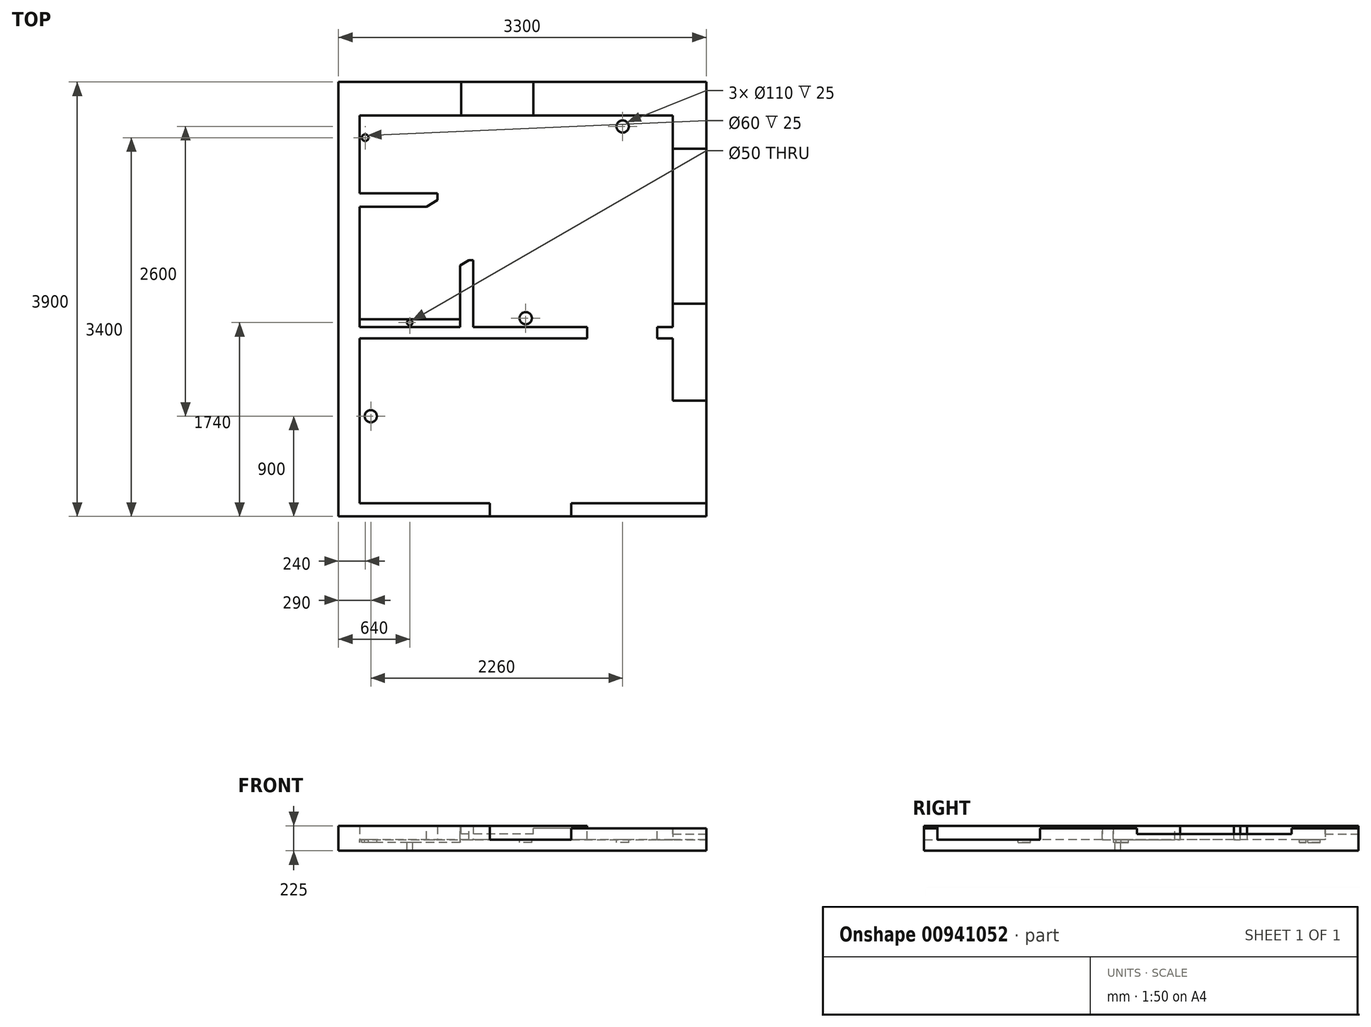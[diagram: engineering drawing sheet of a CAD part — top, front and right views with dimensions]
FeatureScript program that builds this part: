
annotation { "Feature Type Name" : "Feature", "Feature Type Description" : "" }
export const myFeature = defineFeature(function(context is Context, id is Id, definition is map)
    precondition{}
    {
        {
            var Q0;
            Q0=qCreatedBy(makeId("Top.planeOp"),FACE);
            var sketch = newSketch(context, id + "F0", { "sketchPlane" : qUnion([Q0])});
            skLineSegment(sketch, "E0.bottom", {"start": v(0, 0) * mm, "end": v(-3300, 0) * mm});
            skLineSegment(sketch, "E0.top", {"start": v(0, -3900) * mm, "end": v(-3300, -3900) * mm});
            skLineSegment(sketch, "E0.left", {"start": v(0, 0) * mm, "end": v(0, -3900) * mm});
            skLineSegment(sketch, "E0.right", {"start": v(-3300, 0) * mm, "end": v(-3300, -3900) * mm});
            skSolve(sketch);
        }
        {
            var Q0;
            Q0=qSketchRegion(id+"F0",true);
            extrude(context, id + "F1", {"entities" : qUnion([Q0]), "oppositeDirection" : true, "depth" : 100 * mm, "offsetDistance" : 25 * mm});
        }
        {
            var Q0;
            Q0=makeQuery(id+"F0.imprint","IMPRINT",FACE,{"disambiguationData":[TD([[makeQuery(id+"F0.imprint","IMPRINT",EDGE,{"derivedFrom":sQuery(id+"F0.wireOp",EDGE,"E0.bottom")}),1.0]])]});
            var sketch = newSketch(context, id + "F2", { "sketchPlane" : qUnion([Q0])});
            skLineSegment(sketch, "E1.bottom", {"start": v(-300, -300) * mm, "end": v(-1450, -300) * mm});
            skLineSegment(sketch, "E1.top", {"start": v(-300, -2200) * mm, "end": v(-1450, -2200) * mm});
            skLineSegment(sketch, "E1.left", {"start": v(-300, -300) * mm, "end": v(-300, -2200) * mm});
            skLineSegment(sketch, "E1.right", {"start": v(-1450, -300) * mm, "end": v(-1450, -2200) * mm});
            skLineSegment(sketch, "E2.bottom", {"start": v(-1550, -300) * mm, "end": v(-3110, -300) * mm});
            skLineSegment(sketch, "E2.top", {"start": v(-1550, -2200) * mm, "end": v(-3110, -2200) * mm});
            skLineSegment(sketch, "E2.left", {"start": v(-1550, -300) * mm, "end": v(-1550, -2200) * mm});
            skLineSegment(sketch, "E2.right", {"start": v(-3110, -300) * mm, "end": v(-3110, -2200) * mm});
            skLineSegment(sketch, "E3.bottom", {"start": v(-3110, -2300) * mm, "end": v(-300, -2300) * mm});
            skLineSegment(sketch, "E3.top", {"start": v(-3110, -3780) * mm, "end": v(-300, -3780) * mm});
            skLineSegment(sketch, "E3.left", {"start": v(-3110, -2300) * mm, "end": v(-3110, -3780) * mm});
            skLineSegment(sketch, "E3.right", {"start": v(-300, -2300) * mm, "end": v(-300, -3780) * mm});
            skLineSegment(sketch, "E4.bottom", {"start": v(0, 0) * mm, "end": v(-3300, 0) * mm});
            skLineSegment(sketch, "E4.top", {"start": v(0, -3900) * mm, "end": v(-3300, -3900) * mm});
            skLineSegment(sketch, "E4.left", {"start": v(0, 0) * mm, "end": v(0, -3900) * mm});
            skLineSegment(sketch, "E4.right", {"start": v(-3300, 0) * mm, "end": v(-3300, -3900) * mm});
            skSolve(sketch);
        }
        {
            var Q0;
            Q0=qSketchRegion(id+"F2",true);
            extrude(context, id + "F3", {"entities" : qUnion([Q0]), "operationType" : NewBodyOperationType.ADD, "depth" : 100 * mm, "offsetDistance" : 25 * mm});
        }
        {
            var Q0;
            Q0=makeQuery(id+"F3.opExtrude","CAP_FACE",FACE,{"disambiguationData":[OSD([sQuery(id+"F2.wireOp",EDGE,"E1.bottom"),sQuery(id+"F2.wireOp",EDGE,"E1.top"),sQuery(id+"F2.wireOp",EDGE,"E1.left"),sQuery(id+"F2.wireOp",EDGE,"E1.right"),sQuery(id+"F2.wireOp",EDGE,"E2.bottom"),sQuery(id+"F2.wireOp",EDGE,"E2.top"),sQuery(id+"F2.wireOp",EDGE,"E2.left"),sQuery(id+"F2.wireOp",EDGE,"E2.right"),sQuery(id+"F2.wireOp",EDGE,"E3.bottom"),sQuery(id+"F2.wireOp",EDGE,"E3.top"),sQuery(id+"F2.wireOp",EDGE,"E3.left"),sQuery(id+"F2.wireOp",EDGE,"E3.right"),sQuery(id+"F2.wireOp",EDGE,"E4.bottom"),sQuery(id+"F2.wireOp",EDGE,"E4.top"),sQuery(id+"F2.wireOp",EDGE,"E4.left"),sQuery(id+"F2.wireOp",EDGE,"E4.right")])],"isStart":false});
            var sketch = newSketch(context, id + "F4", { "sketchPlane" : qUnion([Q0])});
            skLineSegment(sketch, "E5.bottom", {"start": v(-1550, -300) * mm, "end": v(-2200, -300) * mm});
            skLineSegment(sketch, "E5.top", {"start": v(-1550, 0) * mm, "end": v(-2200, 0) * mm});
            skLineSegment(sketch, "E5.left", {"start": v(-1550, -300) * mm, "end": v(-1550, 0) * mm});
            skLineSegment(sketch, "E5.right", {"start": v(-2200, -300) * mm, "end": v(-2200, 0) * mm});
            skLineSegment(sketch, "E6.bottom", {"start": v(-300, -600) * mm, "end": v(0, -600) * mm});
            skLineSegment(sketch, "E6.top", {"start": v(-300, -1990) * mm, "end": v(0, -1990) * mm});
            skLineSegment(sketch, "E6.left", {"start": v(-300, -600) * mm, "end": v(-300, -1990) * mm});
            skLineSegment(sketch, "E6.right", {"start": v(0, -600) * mm, "end": v(0, -1990) * mm});
            skLineSegment(sketch, "E7.bottom", {"start": v(-440, -2200) * mm, "end": v(-1070, -2200) * mm});
            skLineSegment(sketch, "E7.top", {"start": v(-440, -2300) * mm, "end": v(-1070, -2300) * mm});
            skLineSegment(sketch, "E7.left", {"start": v(-440, -2200) * mm, "end": v(-440, -2300) * mm});
            skLineSegment(sketch, "E7.right", {"start": v(-1070, -2200) * mm, "end": v(-1070, -2300) * mm});
            skLineSegment(sketch, "E8.bottom", {"start": v(-1770, -2200) * mm, "end": v(-2400, -2200) * mm});
            skLineSegment(sketch, "E8.top", {"start": v(-1770, -2300) * mm, "end": v(-2400, -2300) * mm});
            skLineSegment(sketch, "E8.left", {"start": v(-1770, -2200) * mm, "end": v(-1770, -2300) * mm});
            skLineSegment(sketch, "E8.right", {"start": v(-2400, -2200) * mm, "end": v(-2400, -2300) * mm});
            skLineSegment(sketch, "E9.bottom", {"start": v(-1210, -3780) * mm, "end": v(-1940, -3780) * mm});
            skLineSegment(sketch, "E9.top", {"start": v(-1210, -3900) * mm, "end": v(-1940, -3900) * mm});
            skLineSegment(sketch, "E9.left", {"start": v(-1210, -3780) * mm, "end": v(-1210, -3900) * mm});
            skLineSegment(sketch, "E9.right", {"start": v(-1940, -3780) * mm, "end": v(-1940, -3900) * mm});
            skLineSegment(sketch, "E10.bottom", {"start": v(-300, -2860) * mm, "end": v(0, -2860) * mm});
            skLineSegment(sketch, "E10.top", {"start": v(-300, -3780) * mm, "end": v(0, -3780) * mm});
            skLineSegment(sketch, "E10.left", {"start": v(-300, -2860) * mm, "end": v(-300, -3780) * mm});
            skLineSegment(sketch, "E10.right", {"start": v(0, -2860) * mm, "end": v(0, -3780) * mm});
            skSolve(sketch);
        }
        {
            var Q0;
            Q0=makeQuery(id+"F4.imprint","IMPRINT",FACE,{"disambiguationData":[TD([[makeQuery(id+"F4.imprint","IMPRINT",EDGE,{"derivedFrom":sQuery(id+"F4.wireOp",EDGE,"E8.bottom")}),1.0]])]});
            var Q1;
            Q1=makeQuery(id+"F4.imprint","IMPRINT",FACE,{"disambiguationData":[TD([[makeQuery(id+"F4.imprint","IMPRINT",EDGE,{"derivedFrom":sQuery(id+"F4.wireOp",EDGE,"E7.bottom")}),1.0]])]});
            var Q2;
            Q2=makeQuery(id+"F4.imprint","IMPRINT",FACE,{"disambiguationData":[TD([[makeQuery(id+"F4.imprint","IMPRINT",EDGE,{"derivedFrom":sQuery(id+"F4.wireOp",EDGE,"E10.bottom")}),-1.0]])]});
            var Q3;
            Q3=makeQuery(id+"F4.imprint","IMPRINT",FACE,{"disambiguationData":[TD([[makeQuery(id+"F4.imprint","IMPRINT",EDGE,{"derivedFrom":sQuery(id+"F4.wireOp",EDGE,"E9.bottom")}),-1.0]])]});
            var Q4;
            Q4=makeQuery(id+"F3.boolean.opBoolean","SPLIT",FACE,{"disambiguationData":[TD([makeQuery(id+"F3.opExtrude","SWEPT_FACE",FACE,{"disambiguationData":[OSD([sQuery(id+"F2.wireOp",EDGE,"E3.bottom")])]})])],"derivedFrom":makeQuery(id+"F1.opExtrude","CAP_FACE",FACE,{"disambiguationData":[OSD([sQuery(id+"F0.wireOp",EDGE,"E0.bottom"),sQuery(id+"F0.wireOp",EDGE,"E0.top"),sQuery(id+"F0.wireOp",EDGE,"E0.left"),sQuery(id+"F0.wireOp",EDGE,"E0.right")])],"isStart":true})});
            extrude(context, id + "F5", {"entities" : qUnion([Q0, Q1, Q2, Q3]), "operationType" : NewBodyOperationType.REMOVE, "endBound" : BoundingType.UP_TO_SURFACE, "oppositeDirection" : true, "depth" : 25 * mm, "endBoundEntityFace" : qUnion([Q4]), "offsetDistance" : 25 * mm});
        }
        {
            var Q0;
            Q0=makeQuery(id+"F4.imprint","IMPRINT",FACE,{"disambiguationData":[TD([[makeQuery(id+"F4.imprint","IMPRINT",EDGE,{"derivedFrom":sQuery(id+"F4.wireOp",EDGE,"E5.bottom")}),-1.0]])]});
            var Q1;
            Q1=makeQuery(id+"F4.imprint","IMPRINT",FACE,{"disambiguationData":[TD([[makeQuery(id+"F4.imprint","IMPRINT",EDGE,{"derivedFrom":sQuery(id+"F4.wireOp",EDGE,"E6.bottom")}),-1.0]])]});
            extrude(context, id + "F6", {"entities" : qUnion([Q0, Q1]), "operationType" : NewBodyOperationType.REMOVE, "oppositeDirection" : true, "depth" : 50 * mm, "offsetDistance" : 25 * mm});
        }
        {
            var Q0;
            {var subQ0=sQuery(id+"F2.wireOp",EDGE,"E2.left");var subQ2=sQuery(id+"F2.wireOp",EDGE,"E2.top");var subQ4=sQuery(id+"F2.wireOp",EDGE,"E1.right");var subQ6=sQuery(id+"F2.wireOp",EDGE,"E1.left");var subQ9=sQuery(id+"F2.wireOp",EDGE,"E3.bottom");var subQ11=makeQuery(id+"F1.opExtrude","SWEPT_FACE",FACE,{"disambiguationData":[OSD([sQuery(id+"F0.wireOp",EDGE,"E0.bottom")])]});var subQ12=sQuery(id+"F2.wireOp",EDGE,"E1.bottom");var subQ13=makeQuery(id+"F3.opExtrude","SWEPT_FACE",FACE,{"disambiguationData":[OSD([subQ12])]});var subQ15=sQuery(id+"F2.wireOp",EDGE,"E4.bottom");var subQ17=sQuery(id+"F2.wireOp",EDGE,"E1.top");var subQ20=sQuery(id+"F2.wireOp",EDGE,"E4.left");var subQ22=sQuery(id+"F2.wireOp",EDGE,"E3.top");var subQ23=sQuery(id+"F2.wireOp",EDGE,"E4.right");var subQ24=sQuery(id+"F2.wireOp",EDGE,"E4.top");var subQ25=sQuery(id+"F2.wireOp",EDGE,"E3.right");var subQ26=sQuery(id+"F2.wireOp",EDGE,"E3.left");var subQ27=sQuery(id+"F2.wireOp",EDGE,"E2.right");var subQ28=sQuery(id+"F2.wireOp",EDGE,"E2.bottom");Q0=makeQuery(id+"F6.boolean.opBoolean","SPLIT",FACE,{"disambiguationData":[TD([subQ13])],"derivedFrom":makeQuery(id+"F5.boolean.opBoolean","SPLIT",FACE,{"disambiguationData":[TD([subQ11])],"derivedFrom":makeQuery(id+"F3.opExtrude","CAP_FACE",FACE,{"disambiguationData":[OSD([subQ12,subQ17,subQ6,subQ4,subQ28,subQ2,subQ0,subQ27,subQ9,subQ22,subQ26,subQ25,subQ15,subQ24,subQ20,subQ23])],"isStart":false})})});}
            var sketch = newSketch(context, id + "F7", { "sketchPlane" : qUnion([Q0])});
            skLineSegment(sketch, "E11.bottom", {"start": v(-1450, -300) * mm, "end": v(-1550, -300) * mm});
            skLineSegment(sketch, "E11.top", {"start": v(-1450, -2200) * mm, "end": v(-1550, -2200) * mm});
            skLineSegment(sketch, "E11.left", {"start": v(-1450, -300) * mm, "end": v(-1450, -2200) * mm});
            skLineSegment(sketch, "E11.right", {"start": v(-1550, -300) * mm, "end": v(-1550, -2200) * mm});
            skSolve(sketch);
        }
        {
            var Q0;
            Q0 = qSketchRegion(id + "F7", true);
            var Q1;
            {var subQ0=makeQuery(id+"F1.opExtrude","CAP_FACE",FACE,{"disambiguationData":[OSD([sQuery(id+"F0.wireOp",EDGE,"E0.bottom"),sQuery(id+"F0.wireOp",EDGE,"E0.top"),sQuery(id+"F0.wireOp",EDGE,"E0.left"),sQuery(id+"F0.wireOp",EDGE,"E0.right")])],"isStart":true});Q1=makeQuery(id+"F5.boolean.opBoolean","MERGE",FACE,{"derivedFrom":[makeQuery(id+"F3.boolean.opBoolean","SPLIT",FACE,{"disambiguationData":[TD([makeQuery(id+"F3.opExtrude","SWEPT_FACE",FACE,{"disambiguationData":[OSD([sQuery(id+"F2.wireOp",EDGE,"E1.bottom")])]})])],"derivedFrom":subQ0}),makeQuery(id+"F3.boolean.opBoolean","SPLIT",FACE,{"disambiguationData":[TD([makeQuery(id+"F3.opExtrude","SWEPT_FACE",FACE,{"disambiguationData":[OSD([sQuery(id+"F2.wireOp",EDGE,"E2.bottom")])]})])],"derivedFrom":subQ0}),makeQuery(id+"F3.boolean.opBoolean","SPLIT",FACE,{"disambiguationData":[TD([makeQuery(id+"F3.opExtrude","SWEPT_FACE",FACE,{"disambiguationData":[OSD([sQuery(id+"F2.wireOp",EDGE,"E3.bottom")])]})])],"derivedFrom":subQ0})],"fromTools":[makeQuery(id+"F5.opExtrude","CAP_FACE",FACE,{"disambiguationData":[OSD([sQuery(id+"F4.wireOp",EDGE,"E7.bottom"),sQuery(id+"F4.wireOp",EDGE,"E7.top"),sQuery(id+"F4.wireOp",EDGE,"E7.left"),sQuery(id+"F4.wireOp",EDGE,"E7.right")])],"isStart":false}),makeQuery(id+"F5.opExtrude","CAP_FACE",FACE,{"disambiguationData":[OSD([sQuery(id+"F4.wireOp",EDGE,"E8.bottom"),sQuery(id+"F4.wireOp",EDGE,"E8.top"),sQuery(id+"F4.wireOp",EDGE,"E8.left"),sQuery(id+"F4.wireOp",EDGE,"E8.right")])],"isStart":false}),makeQuery(id+"F5.opExtrude","CAP_FACE",FACE,{"disambiguationData":[OSD([sQuery(id+"F4.wireOp",EDGE,"E9.bottom"),sQuery(id+"F4.wireOp",EDGE,"E9.top"),sQuery(id+"F4.wireOp",EDGE,"E9.left"),sQuery(id+"F4.wireOp",EDGE,"E9.right")])],"isStart":false}),makeQuery(id+"F5.opExtrude","CAP_FACE",FACE,{"disambiguationData":[OSD([sQuery(id+"F4.wireOp",EDGE,"E10.bottom"),sQuery(id+"F4.wireOp",EDGE,"E10.top"),sQuery(id+"F4.wireOp",EDGE,"E10.left"),sQuery(id+"F4.wireOp",EDGE,"E10.right")])],"isStart":false})]});}
            extrude(context, id + "F8", {"entities" : qUnion([Q0]), "operationType" : NewBodyOperationType.REMOVE, "endBound" : BoundingType.UP_TO_SURFACE, "oppositeDirection" : true, "depth" : 25 * mm, "endBoundEntityFace" : qUnion([Q1]), "offsetDistance" : 25 * mm});
        }
        {
            var Q0;
            {var subQ0=makeQuery(id+"F1.opExtrude","CAP_FACE",FACE,{"disambiguationData":[OSD([sQuery(id+"F0.wireOp",EDGE,"E0.bottom"),sQuery(id+"F0.wireOp",EDGE,"E0.top"),sQuery(id+"F0.wireOp",EDGE,"E0.left"),sQuery(id+"F0.wireOp",EDGE,"E0.right")])],"isStart":true});Q0=makeQuery(id+"F8.boolean.opBoolean","MERGE",FACE,{"derivedFrom":[makeQuery(id+"F5.boolean.opBoolean","MERGE",FACE,{"derivedFrom":[makeQuery(id+"F3.boolean.opBoolean","SPLIT",FACE,{"disambiguationData":[TD([makeQuery(id+"F3.opExtrude","SWEPT_FACE",FACE,{"disambiguationData":[OSD([sQuery(id+"F2.wireOp",EDGE,"E1.bottom")])]})])],"derivedFrom":subQ0}),makeQuery(id+"F3.boolean.opBoolean","SPLIT",FACE,{"disambiguationData":[TD([makeQuery(id+"F3.opExtrude","SWEPT_FACE",FACE,{"disambiguationData":[OSD([sQuery(id+"F2.wireOp",EDGE,"E2.bottom")])]})])],"derivedFrom":subQ0}),makeQuery(id+"F3.boolean.opBoolean","SPLIT",FACE,{"disambiguationData":[TD([makeQuery(id+"F3.opExtrude","SWEPT_FACE",FACE,{"disambiguationData":[OSD([sQuery(id+"F2.wireOp",EDGE,"E3.bottom")])]})])],"derivedFrom":subQ0})],"fromTools":[makeQuery(id+"F5.opExtrude","CAP_FACE",FACE,{"disambiguationData":[OSD([sQuery(id+"F4.wireOp",EDGE,"E7.bottom"),sQuery(id+"F4.wireOp",EDGE,"E7.top"),sQuery(id+"F4.wireOp",EDGE,"E7.left"),sQuery(id+"F4.wireOp",EDGE,"E7.right")])],"isStart":false}),makeQuery(id+"F5.opExtrude","CAP_FACE",FACE,{"disambiguationData":[OSD([sQuery(id+"F4.wireOp",EDGE,"E8.bottom"),sQuery(id+"F4.wireOp",EDGE,"E8.top"),sQuery(id+"F4.wireOp",EDGE,"E8.left"),sQuery(id+"F4.wireOp",EDGE,"E8.right")])],"isStart":false}),makeQuery(id+"F5.opExtrude","CAP_FACE",FACE,{"disambiguationData":[OSD([sQuery(id+"F4.wireOp",EDGE,"E9.bottom"),sQuery(id+"F4.wireOp",EDGE,"E9.top"),sQuery(id+"F4.wireOp",EDGE,"E9.left"),sQuery(id+"F4.wireOp",EDGE,"E9.right")])],"isStart":false}),makeQuery(id+"F5.opExtrude","CAP_FACE",FACE,{"disambiguationData":[OSD([sQuery(id+"F4.wireOp",EDGE,"E10.bottom"),sQuery(id+"F4.wireOp",EDGE,"E10.top"),sQuery(id+"F4.wireOp",EDGE,"E10.left"),sQuery(id+"F4.wireOp",EDGE,"E10.right")])],"isStart":false})]})],"fromTools":[makeQuery(id+"F8.opExtrude","CAP_FACE",FACE,{"disambiguationData":[OSD([sQuery(id+"F7.wireOp",EDGE,"E11.bottom"),sQuery(id+"F7.wireOp",EDGE,"E11.top"),sQuery(id+"F7.wireOp",EDGE,"E11.left"),sQuery(id+"F7.wireOp",EDGE,"E11.right")])],"isStart":false})]});}
            var sketch = newSketch(context, id + "F9", { "sketchPlane" : qUnion([Q0])});
            skLineSegment(sketch, "E12.bottom", {"start": v(-2400, -2200) * mm, "end": v(-1770, -2200) * mm});
            skLineSegment(sketch, "E12.top", {"start": v(-2400, -2300) * mm, "end": v(-1770, -2300) * mm});
            skLineSegment(sketch, "E12.left", {"start": v(-2400, -2200) * mm, "end": v(-2400, -2300) * mm});
            skLineSegment(sketch, "E12.right", {"start": v(-1770, -2200) * mm, "end": v(-1770, -2300) * mm});
            skSolve(sketch);
        }
        {
            var Q0;
            Q0 = qSketchRegion(id + "F9", true);
            var Q1;
            {var subQ0=sQuery(id+"F2.wireOp",EDGE,"E4.bottom");var subQ2=sQuery(id+"F2.wireOp",EDGE,"E3.left");var subQ4=sQuery(id+"F2.wireOp",EDGE,"E3.top");var subQ6=sQuery(id+"F2.wireOp",EDGE,"E2.right");var subQ8=sQuery(id+"F2.wireOp",EDGE,"E2.top");var subQ11=sQuery(id+"F2.wireOp",EDGE,"E3.bottom");var subQ13=makeQuery(id+"F1.opExtrude","SWEPT_FACE",FACE,{"disambiguationData":[OSD([sQuery(id+"F0.wireOp",EDGE,"E0.bottom")])]});var subQ15=makeQuery(id+"F1.opExtrude","SWEPT_FACE",FACE,{"disambiguationData":[OSD([sQuery(id+"F0.wireOp",EDGE,"E0.top")])]});var subQ16=sQuery(id+"F2.wireOp",EDGE,"E2.bottom");var subQ18=sQuery(id+"F2.wireOp",EDGE,"E4.top");var subQ20=sQuery(id+"F2.wireOp",EDGE,"E4.right");var subQ23=sQuery(id+"F2.wireOp",EDGE,"E4.left");var subQ24=sQuery(id+"F2.wireOp",EDGE,"E3.right");var subQ25=sQuery(id+"F2.wireOp",EDGE,"E2.left");var subQ26=sQuery(id+"F2.wireOp",EDGE,"E1.top");var subQ27=sQuery(id+"F2.wireOp",EDGE,"E1.left");var subQ28=sQuery(id+"F2.wireOp",EDGE,"E1.bottom");var subQ29=sQuery(id+"F2.wireOp",EDGE,"E1.right");Q1=makeQuery(id+"F6.boolean.opBoolean","SPLIT",FACE,{"disambiguationData":[TD([subQ15])],"derivedFrom":makeQuery(id+"F5.boolean.opBoolean","SPLIT",FACE,{"disambiguationData":[TD([subQ13])],"derivedFrom":makeQuery(id+"F3.opExtrude","CAP_FACE",FACE,{"disambiguationData":[OSD([subQ28,subQ26,subQ27,subQ29,subQ16,subQ8,subQ25,subQ6,subQ11,subQ4,subQ2,subQ24,subQ0,subQ18,subQ23,subQ20])],"isStart":false})})});}
            extrude(context, id + "F10", {"entities" : qUnion([Q0]), "operationType" : NewBodyOperationType.ADD, "endBound" : BoundingType.UP_TO_SURFACE, "depth" : 25 * mm, "endBoundEntityFace" : qUnion([Q1]), "offsetDistance" : 25 * mm});
        }
        {
            var Q0;
            {var subQ0=makeQuery(id+"F1.opExtrude","CAP_FACE",FACE,{"disambiguationData":[OSD([sQuery(id+"F0.wireOp",EDGE,"E0.bottom"),sQuery(id+"F0.wireOp",EDGE,"E0.top"),sQuery(id+"F0.wireOp",EDGE,"E0.left"),sQuery(id+"F0.wireOp",EDGE,"E0.right")])],"isStart":true});Q0=makeQuery(id+"F8.boolean.opBoolean","MERGE",FACE,{"derivedFrom":[makeQuery(id+"F5.boolean.opBoolean","MERGE",FACE,{"derivedFrom":[makeQuery(id+"F3.boolean.opBoolean","SPLIT",FACE,{"disambiguationData":[TD([makeQuery(id+"F3.opExtrude","SWEPT_FACE",FACE,{"disambiguationData":[OSD([sQuery(id+"F2.wireOp",EDGE,"E1.bottom")])]})])],"derivedFrom":subQ0}),makeQuery(id+"F3.boolean.opBoolean","SPLIT",FACE,{"disambiguationData":[TD([makeQuery(id+"F3.opExtrude","SWEPT_FACE",FACE,{"disambiguationData":[OSD([sQuery(id+"F2.wireOp",EDGE,"E2.bottom")])]})])],"derivedFrom":subQ0}),makeQuery(id+"F3.boolean.opBoolean","SPLIT",FACE,{"disambiguationData":[TD([makeQuery(id+"F3.opExtrude","SWEPT_FACE",FACE,{"disambiguationData":[OSD([sQuery(id+"F2.wireOp",EDGE,"E3.bottom")])]})])],"derivedFrom":subQ0})],"fromTools":[makeQuery(id+"F5.opExtrude","CAP_FACE",FACE,{"disambiguationData":[OSD([sQuery(id+"F4.wireOp",EDGE,"E7.bottom"),sQuery(id+"F4.wireOp",EDGE,"E7.top"),sQuery(id+"F4.wireOp",EDGE,"E7.left"),sQuery(id+"F4.wireOp",EDGE,"E7.right")])],"isStart":false}),makeQuery(id+"F5.opExtrude","CAP_FACE",FACE,{"disambiguationData":[OSD([sQuery(id+"F4.wireOp",EDGE,"E8.bottom"),sQuery(id+"F4.wireOp",EDGE,"E8.top"),sQuery(id+"F4.wireOp",EDGE,"E8.left"),sQuery(id+"F4.wireOp",EDGE,"E8.right")])],"isStart":false}),makeQuery(id+"F5.opExtrude","CAP_FACE",FACE,{"disambiguationData":[OSD([sQuery(id+"F4.wireOp",EDGE,"E9.bottom"),sQuery(id+"F4.wireOp",EDGE,"E9.top"),sQuery(id+"F4.wireOp",EDGE,"E9.left"),sQuery(id+"F4.wireOp",EDGE,"E9.right")])],"isStart":false}),makeQuery(id+"F5.opExtrude","CAP_FACE",FACE,{"disambiguationData":[OSD([sQuery(id+"F4.wireOp",EDGE,"E10.bottom"),sQuery(id+"F4.wireOp",EDGE,"E10.top"),sQuery(id+"F4.wireOp",EDGE,"E10.left"),sQuery(id+"F4.wireOp",EDGE,"E10.right")])],"isStart":false})]})],"fromTools":[makeQuery(id+"F8.opExtrude","CAP_FACE",FACE,{"disambiguationData":[OSD([sQuery(id+"F7.wireOp",EDGE,"E11.bottom"),sQuery(id+"F7.wireOp",EDGE,"E11.top"),sQuery(id+"F7.wireOp",EDGE,"E11.left"),sQuery(id+"F7.wireOp",EDGE,"E11.right")])],"isStart":false})]});}
            var sketch = newSketch(context, id + "F11", { "sketchPlane" : qUnion([Q0])});
            skLineSegment(sketch, "E13.bottom", {"start": v(-3110, -1000) * mm, "end": v(-2410, -1000) * mm});
            skLineSegment(sketch, "E13.top", {"start": v(-3110, -1120) * mm, "end": v(-2410, -1120) * mm});
            skLineSegment(sketch, "E13.left", {"start": v(-3110, -1000) * mm, "end": v(-3110, -1120) * mm});
            skLineSegment(sketch, "E13.right", {"start": v(-2410, -1000) * mm, "end": v(-2410, -1120) * mm});
            skSolve(sketch);
        }
        {
            var Q0;
            Q0 = qSketchRegion(id + "F11", true);
            var Q1;
            {var subQ2=sQuery(id+"F2.wireOp",EDGE,"E3.bottom");var subQ4=sQuery(id+"F2.wireOp",EDGE,"E2.top");var subQ6=sQuery(id+"F2.wireOp",EDGE,"E1.top");var subQ7=makeQuery(id+"F3.opExtrude","SWEPT_FACE",FACE,{"disambiguationData":[OSD([subQ6])]});var subQ10=sQuery(id+"F2.wireOp",EDGE,"E2.left");var subQ12=sQuery(id+"F2.wireOp",EDGE,"E1.right");var subQ14=sQuery(id+"F2.wireOp",EDGE,"E1.left");var subQ16=makeQuery(id+"F1.opExtrude","SWEPT_FACE",FACE,{"disambiguationData":[OSD([sQuery(id+"F0.wireOp",EDGE,"E0.bottom")])]});var subQ17=sQuery(id+"F2.wireOp",EDGE,"E1.bottom");var subQ18=makeQuery(id+"F3.opExtrude","SWEPT_FACE",FACE,{"disambiguationData":[OSD([subQ17])]});var subQ20=sQuery(id+"F2.wireOp",EDGE,"E4.bottom");var subQ22=sQuery(id+"F2.wireOp",EDGE,"E4.left");var subQ24=sQuery(id+"F2.wireOp",EDGE,"E3.top");var subQ26=sQuery(id+"F2.wireOp",EDGE,"E4.right");var subQ29=sQuery(id+"F2.wireOp",EDGE,"E4.top");var subQ31=sQuery(id+"F2.wireOp",EDGE,"E3.right");var subQ32=sQuery(id+"F2.wireOp",EDGE,"E3.left");var subQ34=sQuery(id+"F2.wireOp",EDGE,"E2.right");var subQ36=makeQuery(id+"F1.opExtrude","SWEPT_FACE",FACE,{"disambiguationData":[OSD([sQuery(id+"F0.wireOp",EDGE,"E0.top")])]});var subQ39=sQuery(id+"F2.wireOp",EDGE,"E2.bottom");var subQ41=makeQuery(id+"F5.boolean.opBoolean","SPLIT",FACE,{"disambiguationData":[TD([subQ16])],"derivedFrom":makeQuery(id+"F3.opExtrude","CAP_FACE",FACE,{"disambiguationData":[OSD([subQ17,subQ6,subQ14,subQ12,subQ39,subQ4,subQ10,subQ34,subQ2,subQ24,subQ32,subQ31,subQ20,subQ29,subQ22,subQ26])],"isStart":false})});Q1=makeQuery(id+"F10.boolean.opBoolean","MERGE",FACE,{"derivedFrom":[makeQuery(id+"F6.boolean.opBoolean","SPLIT",FACE,{"disambiguationData":[TD([subQ36])],"derivedFrom":subQ41}),makeQuery(id+"F8.boolean.opBoolean","SPLIT",FACE,{"disambiguationData":[TD([subQ7])],"derivedFrom":makeQuery(id+"F6.boolean.opBoolean","SPLIT",FACE,{"disambiguationData":[TD([subQ18])],"derivedFrom":subQ41})}),makeQuery(id+"F10.opExtrude","CAP_FACE",FACE,{"disambiguationData":[OSD([sQuery(id+"F9.wireOp",EDGE,"E12.bottom"),sQuery(id+"F9.wireOp",EDGE,"E12.top"),sQuery(id+"F9.wireOp",EDGE,"E12.left"),sQuery(id+"F9.wireOp",EDGE,"E12.right")])],"isStart":false})]});}
            extrude(context, id + "F12", {"entities" : qUnion([Q0]), "operationType" : NewBodyOperationType.ADD, "endBound" : BoundingType.UP_TO_SURFACE, "depth" : 25 * mm, "endBoundEntityFace" : qUnion([Q1]), "offsetDistance" : 25 * mm});
        }
        {
            var Q0;
            {var subQ0=makeQuery(id+"F1.opExtrude","CAP_FACE",FACE,{"disambiguationData":[OSD([sQuery(id+"F0.wireOp",EDGE,"E0.bottom"),sQuery(id+"F0.wireOp",EDGE,"E0.top"),sQuery(id+"F0.wireOp",EDGE,"E0.left"),sQuery(id+"F0.wireOp",EDGE,"E0.right")])],"isStart":true});Q0=makeQuery(id+"F8.boolean.opBoolean","MERGE",FACE,{"derivedFrom":[makeQuery(id+"F5.boolean.opBoolean","MERGE",FACE,{"derivedFrom":[makeQuery(id+"F3.boolean.opBoolean","SPLIT",FACE,{"disambiguationData":[TD([makeQuery(id+"F3.opExtrude","SWEPT_FACE",FACE,{"disambiguationData":[OSD([sQuery(id+"F2.wireOp",EDGE,"E1.bottom")])]})])],"derivedFrom":subQ0}),makeQuery(id+"F3.boolean.opBoolean","SPLIT",FACE,{"disambiguationData":[TD([makeQuery(id+"F3.opExtrude","SWEPT_FACE",FACE,{"disambiguationData":[OSD([sQuery(id+"F2.wireOp",EDGE,"E2.bottom")])]})])],"derivedFrom":subQ0}),makeQuery(id+"F3.boolean.opBoolean","SPLIT",FACE,{"disambiguationData":[TD([makeQuery(id+"F3.opExtrude","SWEPT_FACE",FACE,{"disambiguationData":[OSD([sQuery(id+"F2.wireOp",EDGE,"E3.bottom")])]})])],"derivedFrom":subQ0})],"fromTools":[makeQuery(id+"F5.opExtrude","CAP_FACE",FACE,{"disambiguationData":[OSD([sQuery(id+"F4.wireOp",EDGE,"E7.bottom"),sQuery(id+"F4.wireOp",EDGE,"E7.top"),sQuery(id+"F4.wireOp",EDGE,"E7.left"),sQuery(id+"F4.wireOp",EDGE,"E7.right")])],"isStart":false}),makeQuery(id+"F5.opExtrude","CAP_FACE",FACE,{"disambiguationData":[OSD([sQuery(id+"F4.wireOp",EDGE,"E8.bottom"),sQuery(id+"F4.wireOp",EDGE,"E8.top"),sQuery(id+"F4.wireOp",EDGE,"E8.left"),sQuery(id+"F4.wireOp",EDGE,"E8.right")])],"isStart":false}),makeQuery(id+"F5.opExtrude","CAP_FACE",FACE,{"disambiguationData":[OSD([sQuery(id+"F4.wireOp",EDGE,"E9.bottom"),sQuery(id+"F4.wireOp",EDGE,"E9.top"),sQuery(id+"F4.wireOp",EDGE,"E9.left"),sQuery(id+"F4.wireOp",EDGE,"E9.right")])],"isStart":false}),makeQuery(id+"F5.opExtrude","CAP_FACE",FACE,{"disambiguationData":[OSD([sQuery(id+"F4.wireOp",EDGE,"E10.bottom"),sQuery(id+"F4.wireOp",EDGE,"E10.top"),sQuery(id+"F4.wireOp",EDGE,"E10.left"),sQuery(id+"F4.wireOp",EDGE,"E10.right")])],"isStart":false})]})],"fromTools":[makeQuery(id+"F8.opExtrude","CAP_FACE",FACE,{"disambiguationData":[OSD([sQuery(id+"F7.wireOp",EDGE,"E11.bottom"),sQuery(id+"F7.wireOp",EDGE,"E11.top"),sQuery(id+"F7.wireOp",EDGE,"E11.left"),sQuery(id+"F7.wireOp",EDGE,"E11.right")])],"isStart":false})]});}
            var sketch = newSketch(context, id + "F13", { "sketchPlane" : qUnion([Q0])});
            skLineSegment(sketch, "E14.bottom", {"start": v(-2210, -2200) * mm, "end": v(-2090, -2200) * mm});
            skLineSegment(sketch, "E14.top", {"start": v(-2210, -1600) * mm, "end": v(-2090, -1600) * mm});
            skLineSegment(sketch, "E14.left", {"start": v(-2210, -2200) * mm, "end": v(-2210, -1600) * mm});
            skLineSegment(sketch, "E14.right", {"start": v(-2090, -2200) * mm, "end": v(-2090, -1600) * mm});
            skSolve(sketch);
        }
        {
            var Q0;
            Q0 = qSketchRegion(id + "F13", true);
            var Q1;
            {var subQ2=sQuery(id+"F2.wireOp",EDGE,"E3.bottom");var subQ4=sQuery(id+"F2.wireOp",EDGE,"E2.top");var subQ6=sQuery(id+"F2.wireOp",EDGE,"E1.top");var subQ7=makeQuery(id+"F3.opExtrude","SWEPT_FACE",FACE,{"disambiguationData":[OSD([subQ6])]});var subQ10=sQuery(id+"F2.wireOp",EDGE,"E2.left");var subQ12=sQuery(id+"F2.wireOp",EDGE,"E1.right");var subQ14=sQuery(id+"F2.wireOp",EDGE,"E1.left");var subQ16=makeQuery(id+"F1.opExtrude","SWEPT_FACE",FACE,{"disambiguationData":[OSD([sQuery(id+"F0.wireOp",EDGE,"E0.bottom")])]});var subQ17=sQuery(id+"F2.wireOp",EDGE,"E1.bottom");var subQ18=makeQuery(id+"F3.opExtrude","SWEPT_FACE",FACE,{"disambiguationData":[OSD([subQ17])]});var subQ20=sQuery(id+"F2.wireOp",EDGE,"E4.bottom");var subQ22=sQuery(id+"F2.wireOp",EDGE,"E4.left");var subQ24=sQuery(id+"F2.wireOp",EDGE,"E3.top");var subQ26=sQuery(id+"F2.wireOp",EDGE,"E4.right");var subQ29=sQuery(id+"F2.wireOp",EDGE,"E4.top");var subQ31=sQuery(id+"F2.wireOp",EDGE,"E3.right");var subQ32=sQuery(id+"F2.wireOp",EDGE,"E3.left");var subQ34=sQuery(id+"F2.wireOp",EDGE,"E2.right");var subQ36=makeQuery(id+"F1.opExtrude","SWEPT_FACE",FACE,{"disambiguationData":[OSD([sQuery(id+"F0.wireOp",EDGE,"E0.top")])]});var subQ39=sQuery(id+"F2.wireOp",EDGE,"E2.bottom");var subQ41=makeQuery(id+"F5.boolean.opBoolean","SPLIT",FACE,{"disambiguationData":[TD([subQ16])],"derivedFrom":makeQuery(id+"F3.opExtrude","CAP_FACE",FACE,{"disambiguationData":[OSD([subQ17,subQ6,subQ14,subQ12,subQ39,subQ4,subQ10,subQ34,subQ2,subQ24,subQ32,subQ31,subQ20,subQ29,subQ22,subQ26])],"isStart":false})});Q1=makeQuery(id+"F12.boolean.opBoolean","MERGE",FACE,{"derivedFrom":[makeQuery(id+"F10.boolean.opBoolean","MERGE",FACE,{"derivedFrom":[makeQuery(id+"F6.boolean.opBoolean","SPLIT",FACE,{"disambiguationData":[TD([subQ36])],"derivedFrom":subQ41}),makeQuery(id+"F8.boolean.opBoolean","SPLIT",FACE,{"disambiguationData":[TD([subQ7])],"derivedFrom":makeQuery(id+"F6.boolean.opBoolean","SPLIT",FACE,{"disambiguationData":[TD([subQ18])],"derivedFrom":subQ41})}),makeQuery(id+"F10.opExtrude","CAP_FACE",FACE,{"disambiguationData":[OSD([sQuery(id+"F9.wireOp",EDGE,"E12.bottom"),sQuery(id+"F9.wireOp",EDGE,"E12.top"),sQuery(id+"F9.wireOp",EDGE,"E12.left"),sQuery(id+"F9.wireOp",EDGE,"E12.right")])],"isStart":false})]}),makeQuery(id+"F12.opExtrude","CAP_FACE",FACE,{"disambiguationData":[OSD([sQuery(id+"F11.wireOp",EDGE,"E13.bottom"),sQuery(id+"F11.wireOp",EDGE,"E13.top"),sQuery(id+"F11.wireOp",EDGE,"E13.left"),sQuery(id+"F11.wireOp",EDGE,"E13.right")])],"isStart":false})]});}
            extrude(context, id + "F14", {"entities" : qUnion([Q0]), "operationType" : NewBodyOperationType.ADD, "endBound" : BoundingType.UP_TO_SURFACE, "depth" : 25 * mm, "endBoundEntityFace" : qUnion([Q1]), "offsetDistance" : 25 * mm});
        }
        {
            var Q0;
            {var subQ2=sQuery(id+"F2.wireOp",EDGE,"E3.bottom");var subQ4=sQuery(id+"F2.wireOp",EDGE,"E2.top");var subQ6=sQuery(id+"F2.wireOp",EDGE,"E1.top");var subQ7=makeQuery(id+"F3.opExtrude","SWEPT_FACE",FACE,{"disambiguationData":[OSD([subQ6])]});var subQ10=sQuery(id+"F2.wireOp",EDGE,"E2.left");var subQ12=sQuery(id+"F2.wireOp",EDGE,"E1.right");var subQ14=sQuery(id+"F2.wireOp",EDGE,"E1.left");var subQ16=makeQuery(id+"F1.opExtrude","SWEPT_FACE",FACE,{"disambiguationData":[OSD([sQuery(id+"F0.wireOp",EDGE,"E0.bottom")])]});var subQ17=sQuery(id+"F2.wireOp",EDGE,"E1.bottom");var subQ18=makeQuery(id+"F3.opExtrude","SWEPT_FACE",FACE,{"disambiguationData":[OSD([subQ17])]});var subQ20=sQuery(id+"F2.wireOp",EDGE,"E4.bottom");var subQ22=sQuery(id+"F2.wireOp",EDGE,"E4.left");var subQ24=sQuery(id+"F2.wireOp",EDGE,"E3.top");var subQ26=sQuery(id+"F2.wireOp",EDGE,"E4.right");var subQ29=sQuery(id+"F2.wireOp",EDGE,"E4.top");var subQ31=sQuery(id+"F2.wireOp",EDGE,"E3.right");var subQ32=sQuery(id+"F2.wireOp",EDGE,"E3.left");var subQ34=sQuery(id+"F2.wireOp",EDGE,"E2.right");var subQ36=makeQuery(id+"F1.opExtrude","SWEPT_FACE",FACE,{"disambiguationData":[OSD([sQuery(id+"F0.wireOp",EDGE,"E0.top")])]});var subQ39=sQuery(id+"F2.wireOp",EDGE,"E2.bottom");var subQ41=makeQuery(id+"F5.boolean.opBoolean","SPLIT",FACE,{"disambiguationData":[TD([subQ16])],"derivedFrom":makeQuery(id+"F3.opExtrude","CAP_FACE",FACE,{"disambiguationData":[OSD([subQ17,subQ6,subQ14,subQ12,subQ39,subQ4,subQ10,subQ34,subQ2,subQ24,subQ32,subQ31,subQ20,subQ29,subQ22,subQ26])],"isStart":false})});Q0=makeQuery(id+"F14.boolean.opBoolean","MERGE",FACE,{"derivedFrom":[makeQuery(id+"F12.boolean.opBoolean","MERGE",FACE,{"derivedFrom":[makeQuery(id+"F10.boolean.opBoolean","MERGE",FACE,{"derivedFrom":[makeQuery(id+"F6.boolean.opBoolean","SPLIT",FACE,{"disambiguationData":[TD([subQ36])],"derivedFrom":subQ41}),makeQuery(id+"F8.boolean.opBoolean","SPLIT",FACE,{"disambiguationData":[TD([subQ7])],"derivedFrom":makeQuery(id+"F6.boolean.opBoolean","SPLIT",FACE,{"disambiguationData":[TD([subQ18])],"derivedFrom":subQ41})}),makeQuery(id+"F10.opExtrude","CAP_FACE",FACE,{"disambiguationData":[OSD([sQuery(id+"F9.wireOp",EDGE,"E12.bottom"),sQuery(id+"F9.wireOp",EDGE,"E12.top"),sQuery(id+"F9.wireOp",EDGE,"E12.left"),sQuery(id+"F9.wireOp",EDGE,"E12.right")])],"isStart":false})]}),makeQuery(id+"F12.opExtrude","CAP_FACE",FACE,{"disambiguationData":[OSD([sQuery(id+"F11.wireOp",EDGE,"E13.bottom"),sQuery(id+"F11.wireOp",EDGE,"E13.top"),sQuery(id+"F11.wireOp",EDGE,"E13.left"),sQuery(id+"F11.wireOp",EDGE,"E13.right")])],"isStart":false})]}),makeQuery(id+"F14.opExtrude","CAP_FACE",FACE,{"disambiguationData":[OSD([sQuery(id+"F13.wireOp",EDGE,"E14.bottom"),sQuery(id+"F13.wireOp",EDGE,"E14.top"),sQuery(id+"F13.wireOp",EDGE,"E14.left"),sQuery(id+"F13.wireOp",EDGE,"E14.right")])],"isStart":false})]});}
            extrude(context, id + "F15", {"entities" : qUnion([Q0]), "operationType" : NewBodyOperationType.ADD, "depth" : 25 * mm, "offsetDistance" : 25 * mm});
        }
        {
            var Q0;
            Q0=makeQuery(id+"F15.opExtrude","CAP_FACE",FACE,{"disambiguationData":[OSD([sQuery(id+"F2.wireOp",EDGE,"E1.bottom"),sQuery(id+"F2.wireOp",EDGE,"E1.top"),sQuery(id+"F2.wireOp",EDGE,"E1.left"),sQuery(id+"F2.wireOp",EDGE,"E1.right"),sQuery(id+"F2.wireOp",EDGE,"E2.bottom"),sQuery(id+"F2.wireOp",EDGE,"E2.top"),sQuery(id+"F2.wireOp",EDGE,"E2.left"),sQuery(id+"F2.wireOp",EDGE,"E2.right"),sQuery(id+"F2.wireOp",EDGE,"E3.bottom"),sQuery(id+"F2.wireOp",EDGE,"E3.top"),sQuery(id+"F2.wireOp",EDGE,"E3.left"),sQuery(id+"F2.wireOp",EDGE,"E3.right"),sQuery(id+"F2.wireOp",EDGE,"E4.bottom"),sQuery(id+"F2.wireOp",EDGE,"E4.top"),sQuery(id+"F2.wireOp",EDGE,"E4.left"),sQuery(id+"F2.wireOp",EDGE,"E4.right"),sQuery(id+"F9.wireOp",EDGE,"E12.bottom"),sQuery(id+"F9.wireOp",EDGE,"E12.top"),sQuery(id+"F9.wireOp",EDGE,"E12.left"),sQuery(id+"F9.wireOp",EDGE,"E12.right"),sQuery(id+"F11.wireOp",EDGE,"E13.bottom"),sQuery(id+"F11.wireOp",EDGE,"E13.top"),sQuery(id+"F11.wireOp",EDGE,"E13.left"),sQuery(id+"F11.wireOp",EDGE,"E13.right"),sQuery(id+"F13.wireOp",EDGE,"E14.bottom"),sQuery(id+"F13.wireOp",EDGE,"E14.top"),sQuery(id+"F13.wireOp",EDGE,"E14.left"),sQuery(id+"F13.wireOp",EDGE,"E14.right")])],"isStart":false});
            var sketch = newSketch(context, id + "F16", { "sketchPlane" : qUnion([Q0])});
            skLineSegment(sketch, "E15", {"start": v(-2410, -1060) * mm, "end": v(-2510, -1120) * mm});
            skLineSegment(sketch, "E16", {"start": v(-2510, -1120) * mm, "end": v(-2410, -1120) * mm});
            skLineSegment(sketch, "E17", {"start": v(-2410, -1120) * mm, "end": v(-2410, -1060) * mm});
            skLineSegment(sketch, "E18", {"start": v(-2130, -1600) * mm, "end": v(-2210, -1600) * mm});
            skLineSegment(sketch, "E19", {"start": v(-2210, -1600) * mm, "end": v(-2210, -1648) * mm});
            skLineSegment(sketch, "E20", {"start": v(-2210, -1648) * mm, "end": v(-2130, -1600) * mm});
            skPoint(sketch, "E21.startSnap0", {"position": v(-2410, -1060) * mm});
            skPoint(sketch, "E21.startSnap1", {"position": v(-2460, -1090) * mm});
            skLineSegment(sketch, "E22", {"start": v(-2469.02, -1095.4) * mm, "end": v(-2156.66, -1616) * mm, "construction": true});
            skSolve(sketch);
        }
        {
            var Q0;
            Q0 = qSketchRegion(id + "F16", true);
            var Q1;
            {var subQ0=makeQuery(id+"F1.opExtrude","CAP_FACE",FACE,{"disambiguationData":[OSD([sQuery(id+"F0.wireOp",EDGE,"E0.bottom"),sQuery(id+"F0.wireOp",EDGE,"E0.top"),sQuery(id+"F0.wireOp",EDGE,"E0.left"),sQuery(id+"F0.wireOp",EDGE,"E0.right")])],"isStart":true});Q1=makeQuery(id+"F8.boolean.opBoolean","MERGE",FACE,{"derivedFrom":[makeQuery(id+"F5.boolean.opBoolean","MERGE",FACE,{"derivedFrom":[makeQuery(id+"F3.boolean.opBoolean","SPLIT",FACE,{"disambiguationData":[TD([makeQuery(id+"F3.opExtrude","SWEPT_FACE",FACE,{"disambiguationData":[OSD([sQuery(id+"F2.wireOp",EDGE,"E1.bottom")])]})])],"derivedFrom":subQ0}),makeQuery(id+"F3.boolean.opBoolean","SPLIT",FACE,{"disambiguationData":[TD([makeQuery(id+"F3.opExtrude","SWEPT_FACE",FACE,{"disambiguationData":[OSD([sQuery(id+"F2.wireOp",EDGE,"E2.bottom")])]})])],"derivedFrom":subQ0}),makeQuery(id+"F3.boolean.opBoolean","SPLIT",FACE,{"disambiguationData":[TD([makeQuery(id+"F3.opExtrude","SWEPT_FACE",FACE,{"disambiguationData":[OSD([sQuery(id+"F2.wireOp",EDGE,"E3.bottom")])]})])],"derivedFrom":subQ0})],"fromTools":[makeQuery(id+"F5.opExtrude","CAP_FACE",FACE,{"disambiguationData":[OSD([sQuery(id+"F4.wireOp",EDGE,"E7.bottom"),sQuery(id+"F4.wireOp",EDGE,"E7.top"),sQuery(id+"F4.wireOp",EDGE,"E7.left"),sQuery(id+"F4.wireOp",EDGE,"E7.right")])],"isStart":false}),makeQuery(id+"F5.opExtrude","CAP_FACE",FACE,{"disambiguationData":[OSD([sQuery(id+"F4.wireOp",EDGE,"E8.bottom"),sQuery(id+"F4.wireOp",EDGE,"E8.top"),sQuery(id+"F4.wireOp",EDGE,"E8.left"),sQuery(id+"F4.wireOp",EDGE,"E8.right")])],"isStart":false}),makeQuery(id+"F5.opExtrude","CAP_FACE",FACE,{"disambiguationData":[OSD([sQuery(id+"F4.wireOp",EDGE,"E9.bottom"),sQuery(id+"F4.wireOp",EDGE,"E9.top"),sQuery(id+"F4.wireOp",EDGE,"E9.left"),sQuery(id+"F4.wireOp",EDGE,"E9.right")])],"isStart":false}),makeQuery(id+"F5.opExtrude","CAP_FACE",FACE,{"disambiguationData":[OSD([sQuery(id+"F4.wireOp",EDGE,"E10.bottom"),sQuery(id+"F4.wireOp",EDGE,"E10.top"),sQuery(id+"F4.wireOp",EDGE,"E10.left"),sQuery(id+"F4.wireOp",EDGE,"E10.right")])],"isStart":false})]})],"fromTools":[makeQuery(id+"F8.opExtrude","CAP_FACE",FACE,{"disambiguationData":[OSD([sQuery(id+"F7.wireOp",EDGE,"E11.bottom"),sQuery(id+"F7.wireOp",EDGE,"E11.top"),sQuery(id+"F7.wireOp",EDGE,"E11.left"),sQuery(id+"F7.wireOp",EDGE,"E11.right")])],"isStart":false})]});}
            extrude(context, id + "F17", {"entities" : qUnion([Q0]), "operationType" : NewBodyOperationType.REMOVE, "endBound" : BoundingType.UP_TO_SURFACE, "oppositeDirection" : true, "depth" : 25 * mm, "endBoundEntityFace" : qUnion([Q1]), "offsetDistance" : 25 * mm});
        }
        {
            var Q0;
            {var subQ0=makeQuery(id+"F1.opExtrude","CAP_FACE",FACE,{"disambiguationData":[OSD([sQuery(id+"F0.wireOp",EDGE,"E0.bottom"),sQuery(id+"F0.wireOp",EDGE,"E0.top"),sQuery(id+"F0.wireOp",EDGE,"E0.left"),sQuery(id+"F0.wireOp",EDGE,"E0.right")])],"isStart":true});Q0=makeQuery(id+"F17.boolean.opBoolean","MERGE",FACE,{"derivedFrom":[makeQuery(id+"F8.boolean.opBoolean","MERGE",FACE,{"derivedFrom":[makeQuery(id+"F5.boolean.opBoolean","MERGE",FACE,{"derivedFrom":[makeQuery(id+"F3.boolean.opBoolean","SPLIT",FACE,{"disambiguationData":[TD([makeQuery(id+"F3.opExtrude","SWEPT_FACE",FACE,{"disambiguationData":[OSD([sQuery(id+"F2.wireOp",EDGE,"E1.bottom")])]})])],"derivedFrom":subQ0}),makeQuery(id+"F3.boolean.opBoolean","SPLIT",FACE,{"disambiguationData":[TD([makeQuery(id+"F3.opExtrude","SWEPT_FACE",FACE,{"disambiguationData":[OSD([sQuery(id+"F2.wireOp",EDGE,"E2.bottom")])]})])],"derivedFrom":subQ0}),makeQuery(id+"F3.boolean.opBoolean","SPLIT",FACE,{"disambiguationData":[TD([makeQuery(id+"F3.opExtrude","SWEPT_FACE",FACE,{"disambiguationData":[OSD([sQuery(id+"F2.wireOp",EDGE,"E3.bottom")])]})])],"derivedFrom":subQ0})],"fromTools":[makeQuery(id+"F5.opExtrude","CAP_FACE",FACE,{"disambiguationData":[OSD([sQuery(id+"F4.wireOp",EDGE,"E7.bottom"),sQuery(id+"F4.wireOp",EDGE,"E7.top"),sQuery(id+"F4.wireOp",EDGE,"E7.left"),sQuery(id+"F4.wireOp",EDGE,"E7.right")])],"isStart":false}),makeQuery(id+"F5.opExtrude","CAP_FACE",FACE,{"disambiguationData":[OSD([sQuery(id+"F4.wireOp",EDGE,"E8.bottom"),sQuery(id+"F4.wireOp",EDGE,"E8.top"),sQuery(id+"F4.wireOp",EDGE,"E8.left"),sQuery(id+"F4.wireOp",EDGE,"E8.right")])],"isStart":false}),makeQuery(id+"F5.opExtrude","CAP_FACE",FACE,{"disambiguationData":[OSD([sQuery(id+"F4.wireOp",EDGE,"E9.bottom"),sQuery(id+"F4.wireOp",EDGE,"E9.top"),sQuery(id+"F4.wireOp",EDGE,"E9.left"),sQuery(id+"F4.wireOp",EDGE,"E9.right")])],"isStart":false}),makeQuery(id+"F5.opExtrude","CAP_FACE",FACE,{"disambiguationData":[OSD([sQuery(id+"F4.wireOp",EDGE,"E10.bottom"),sQuery(id+"F4.wireOp",EDGE,"E10.top"),sQuery(id+"F4.wireOp",EDGE,"E10.left"),sQuery(id+"F4.wireOp",EDGE,"E10.right")])],"isStart":false})]})],"fromTools":[makeQuery(id+"F8.opExtrude","CAP_FACE",FACE,{"disambiguationData":[OSD([sQuery(id+"F7.wireOp",EDGE,"E11.bottom"),sQuery(id+"F7.wireOp",EDGE,"E11.top"),sQuery(id+"F7.wireOp",EDGE,"E11.left"),sQuery(id+"F7.wireOp",EDGE,"E11.right")])],"isStart":false})]})],"fromTools":[makeQuery(id+"F17.opExtrude","CAP_FACE",FACE,{"disambiguationData":[OSD([sQuery(id+"F16.wireOp",EDGE,"E15"),sQuery(id+"F16.wireOp",EDGE,"E16"),sQuery(id+"F16.wireOp",EDGE,"E17")])],"isStart":false}),makeQuery(id+"F17.opExtrude","CAP_FACE",FACE,{"disambiguationData":[OSD([sQuery(id+"F16.wireOp",EDGE,"E18"),sQuery(id+"F16.wireOp",EDGE,"E19"),sQuery(id+"F16.wireOp",EDGE,"E20")])],"isStart":false})]});}
            var sketch = newSketch(context, id + "F18", { "sketchPlane" : qUnion([Q0])});
            skCircle(sketch, "E23", {"center": v(-750, -400) * mm, "radius": 55 * mm});
            skCircle(sketch, "E24", {"center": v(-3060, -500) * mm, "radius": 30 * mm});
            skCircle(sketch, "E25", {"center": v(-1620, -2120) * mm, "radius": 55 * mm});
            skCircle(sketch, "E26", {"center": v(-3010, -3000) * mm, "radius": 55 * mm});
            skLineSegment(sketch, "E27.bottom", {"start": v(-3110, -2130) * mm, "end": v(-2210, -2130) * mm});
            skLineSegment(sketch, "E27.top", {"start": v(-3110, -2200) * mm, "end": v(-2210, -2200) * mm});
            skLineSegment(sketch, "E27.left", {"start": v(-3110, -2130) * mm, "end": v(-3110, -2200) * mm});
            skLineSegment(sketch, "E27.right", {"start": v(-2210, -2130) * mm, "end": v(-2210, -2200) * mm});
            skSolve(sketch);
        }
        {
            var Q0;
            Q0 = qSketchRegion(id + "F18", true);
            extrude(context, id + "F19", {"entities" : qUnion([Q0]), "operationType" : NewBodyOperationType.REMOVE, "oppositeDirection" : true, "depth" : 25 * mm, "offsetDistance" : 25 * mm});
        }
        {
            var Q0;
            Q0=makeQuery(id+"F18.imprint","IMPRINT",FACE,{"disambiguationData":[TD([[makeQuery(id+"F18.imprint","IMPRINT",EDGE,{"derivedFrom":sQuery(id+"F18.wireOp",EDGE,"E27.bottom")}),-1.0]])]});
            var sketch = newSketch(context, id + "F20", { "sketchPlane" : qUnion([Q0])});
            skCircle(sketch, "E28", {"center": v(-2660, -2160) * mm, "radius": 25 * mm});
            skSolve(sketch);
        }
        {
            var Q0;
            Q0 = qSketchRegion(id + "F20", true);
            extrude(context, id + "F21", {"entities" : qUnion([Q0]), "operationType" : NewBodyOperationType.REMOVE, "oppositeDirection" : true, "depth" : 100 * mm, "offsetDistance" : 25 * mm});
        }
    });
